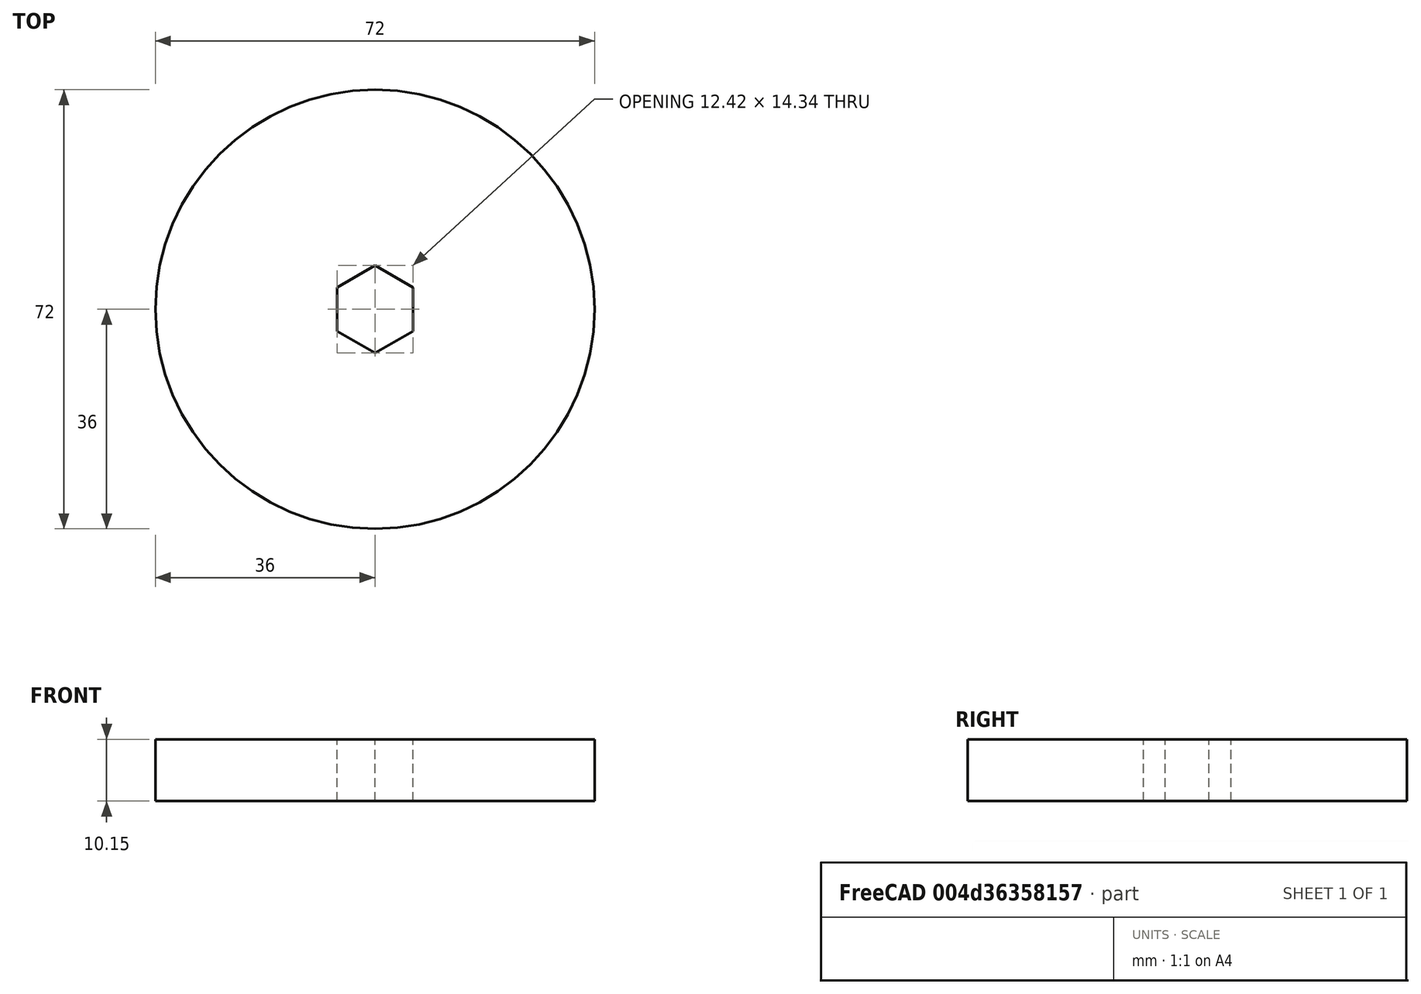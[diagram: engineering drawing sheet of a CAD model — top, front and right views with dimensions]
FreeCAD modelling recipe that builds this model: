
FCSTD DOCUMENT  (FreeCAD 0.16R6707 (Git))
Label: roue bleue
License: All rights reserved
LicenseURL: http://en.wikipedia.org/wiki/All_rights_reserved
objects: Sketcher::SketchObject×1, PartDesign::Pad×1
note: 3 computed .brp shape members not serialized (recipe doc carries the construction recipe); baked Part::Feature solids carry a one-line shape summary decoded from their .brp

FEATURE [Sketcher::SketchObject] Sketch
  sketch-geometry (9):
    g0: Circle CenterX=0 CenterY=0 CenterZ=0 NormalX=0 NormalY=0 NormalZ=1 Radius=36
    g1: GeomPoint [constr] X=0 Y=7.17 Z=0
    g2: LineSegment StartX=0 StartY=7.17 StartZ=0 EndX=-6.2094 EndY=3.585 EndZ=0
    g3: LineSegment StartX=-6.2094 StartY=3.585 StartZ=0 EndX=-6.2094 EndY=-3.585 EndZ=0
    g4: LineSegment StartX=-6.2094 StartY=-3.585 StartZ=0 EndX=0 EndY=-7.17 EndZ=0
    g5: LineSegment StartX=0 StartY=-7.17 StartZ=0 EndX=6.2094 EndY=-3.585 EndZ=0
    g6: LineSegment StartX=6.2094 StartY=-3.585 StartZ=0 EndX=6.2094 EndY=3.585 EndZ=0
    g7: LineSegment StartX=6.2094 StartY=3.585 StartZ=0 EndX=0 EndY=7.17 EndZ=0
    g8: Circle [constr] CenterX=0 CenterY=0 CenterZ=0 NormalX=0 NormalY=0 NormalZ=1 Radius=7.17
  constraints (19):
    c: Coincident(g0,g-1)
    c: Radius(g0) = 36
    c: PointOnObject(g1,g-2)
    c: DistanceY(g1) = 7.17
    c: Coincident(g2,g3)
    c: Coincident(g3,g4)
    c: Coincident(g4,g5)
    c: Coincident(g5,g6)
    c: Coincident(g6,g7)
    c: Coincident(g7,g2)
    c: Equal(g2, g3-g7) x5
    c: PointOnObject(g2,g8)
    c: PointOnObject(g3,g8)
    c: PointOnObject(g4,g8)
    c: PointOnObject(g5,g8)
    c: PointOnObject(g6,g8)
    c: PointOnObject(g7,g8)
    c: Coincident(g8,g-1)
    c: Coincident(g7,g1)
FEATURE [PartDesign::Pad] Pad
  Length = 10.15
  Length2 = 100
  Sketch = -> Sketch
  Type = 0
